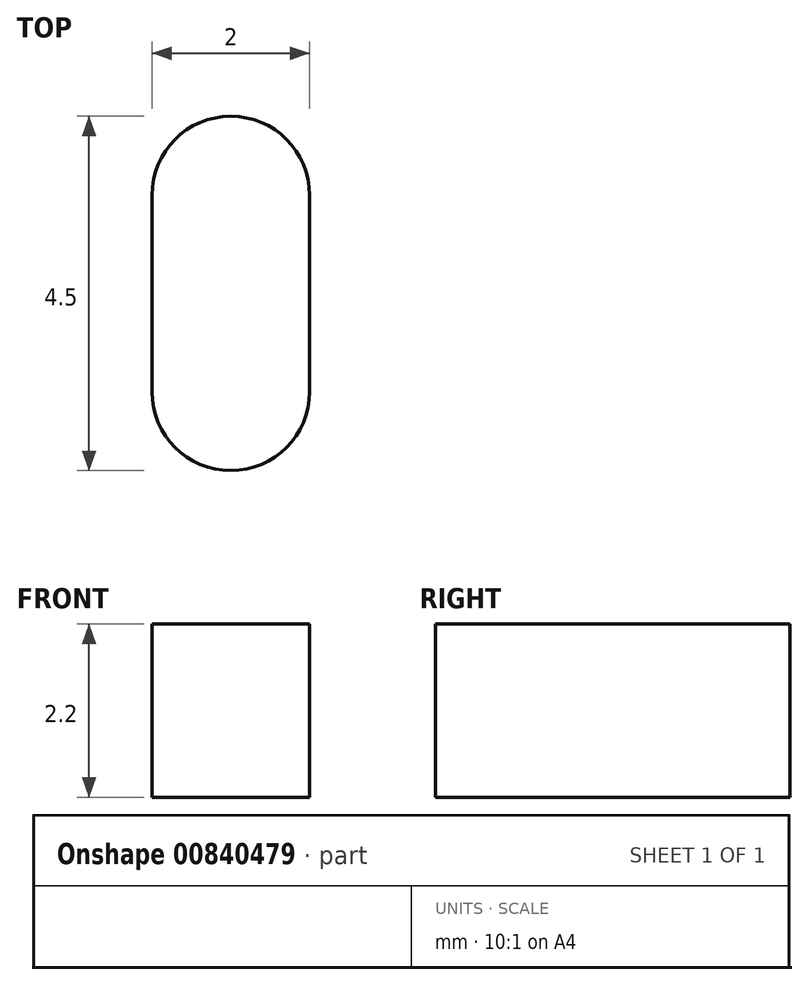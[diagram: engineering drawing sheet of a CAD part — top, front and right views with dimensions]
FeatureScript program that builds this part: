
annotation { "Feature Type Name" : "Feature", "Feature Type Description" : "" }
export const myFeature = defineFeature(function(context is Context, id is Id, definition is map)
    precondition{}
    {
        {
            var Q0;
            Q0=qCreatedBy(makeId("Top.planeOp"),FACE);
            var sketch = newSketch(context, id + "F0", { "sketchPlane" : qUnion([Q0])});
            skArc(sketch, "E0", {"start": v(1, 2.5) * mm, "mid": v(0, 3.5) * mm, "end": v(-1, 2.5) * mm});
            skArc(sketch, "E1", {"start": v(-1, 0) * mm, "mid": v(0, -1) * mm, "end": v(1, 0) * mm});
            skLineSegment(sketch, "E2", {"start": v(-1, 2.5) * mm, "end": v(-1, 0) * mm});
            skLineSegment(sketch, "E3", {"start": v(1, 2.5) * mm, "end": v(1, 0) * mm});
            skSolve(sketch);
        }
        {
            var Q0;
            Q0=makeQuery(id+"F0.imprint","IMPRINT",FACE,{"disambiguationData":[TD([[makeQuery(id+"F0.imprint","IMPRINT",EDGE,{"derivedFrom":sQuery(id+"F0.wireOp",EDGE,"E0")}),1.0]])]});
            extrude(context, id + "F1", {"entities" : qUnion([Q0]), "depth" : 2.2 * mm, "offsetDistance" : 25 * mm});
        }
    });
